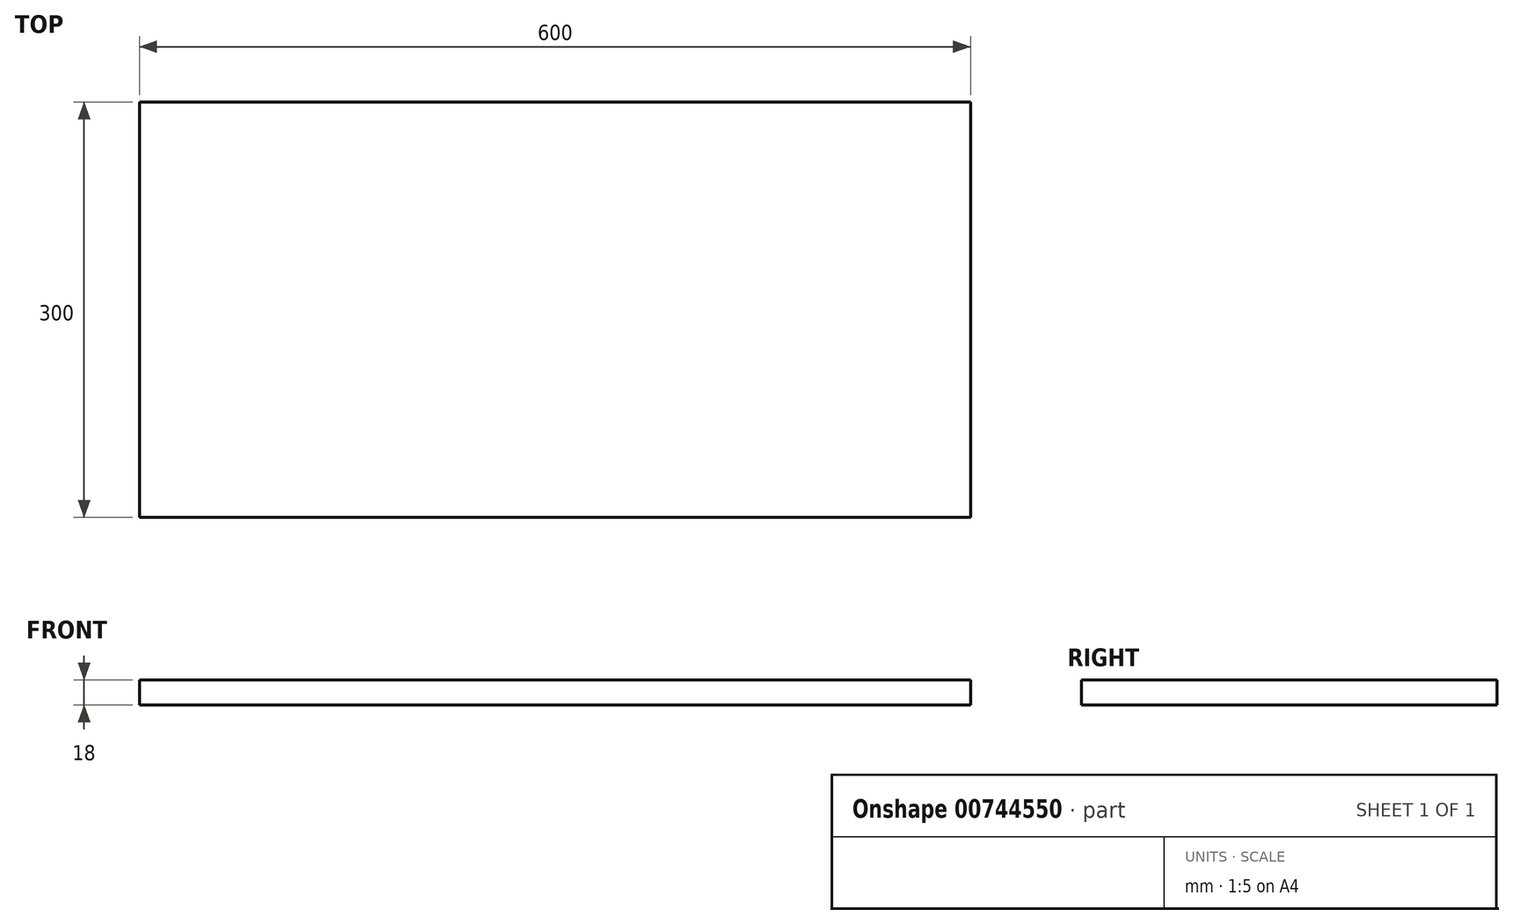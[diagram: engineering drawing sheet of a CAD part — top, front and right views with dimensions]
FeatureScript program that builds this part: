
annotation { "Feature Type Name" : "Feature", "Feature Type Description" : "" }
export const myFeature = defineFeature(function(context is Context, id is Id, definition is map)
    precondition{}
    {
        {
            var Q0;
            Q0=qCreatedBy(makeId("Top.planeOp"),FACE);
            var sketch = newSketch(context, id + "F0", { "sketchPlane" : qUnion([Q0])});
            skLineSegment(sketch, "E0.bottom", {"start": v(-300, -100) * mm, "end": v(300, -100) * mm});
            skLineSegment(sketch, "E0.top", {"start": v(-300, 200) * mm, "end": v(300, 200) * mm});
            skLineSegment(sketch, "E0.left", {"start": v(-300, -100) * mm, "end": v(-300, 200) * mm});
            skLineSegment(sketch, "E0.right", {"start": v(300, -100) * mm, "end": v(300, 200) * mm});
            skLineSegment(sketch, "E1", {"start": v(-300, 0) * mm, "end": v(300, 0) * mm, "construction": true});
            skLineSegment(sketch, "E2", {"start": v(0, 200) * mm, "end": v(0, -100) * mm, "construction": true});
            skSolve(sketch);
        }
        {
            var Q0;
            Q0 = qSketchRegion(id + "F0", true);
            extrude(context, id + "F1", {"entities" : qUnion([Q0]), "oppositeDirection" : true, "depth" : 18 * mm, "offsetDistance" : 25 * mm});
        }
    });
